# Revit family: 0005337
name_source: partatom
category: Lighting Fixtures
revit_build: Autodesk Revit 2017 (Build: 20190507_1515(x64)
units: mm (PartAtom-declared; Revit-internal decimal feet)

## family parameters
Cut with Voids When Loaded = No
Host = Face
Light Source = No
OmniClass Number = 23.80.70.00
OmniClass Title = Lighting
Part Type = Normal
Room Calculation Point = No
Round Connector Dimension = Use Diameter
Shared = No

## types (4) — shared parameters
Apparent Load = 0 VA
Assembly Code = D5020200
AssetType = Fixed
ClassificationName = Uniclass2015
ClassificationValue = EF_70_80
Default Elevation = 1219 mm
DocumentationLiterature = http://www.sylvania-lighting.com
IfcExportAs = IfcLightFixtureType
IfcExportType = IfcLightFixtureType
ImpactProtectionIndex = IK03
IngressProtection = IP20
InputNominalFrequency = 50/60 Hz
InputVoltage = 220-240 V AC
Keynote = 16500
Lamp = LED
LampColourRenderingIndex = 90
LampMacAdamStep = 3
LampsType = LED
Manufacturer = Feilo Sylvania
ManufacturerName = Feilo Sylvania
Material = aluminium housing
Material_1_SYL = PC/ABS Plastic
Material_2_SYL = <By Category>
Material_3_SYL = <By Category>
Material_4_SYL = <By Category>
NominalDepth = 180 mm
NominalLength = 180 mm
PowerFactor = 0.9
RadiusTrim_SYL = 90 mm  [stored 0.295276 ft]
RecessDepth_SYL = 100 mm  [stored 0.328084 ft]
RecessRadius_SYL = 83 mm
TrimHeight_SYL = 3 mm  [stored 0.00984252 ft]
Type Image = <None>
URL = http://www.sylvania-lighting.com
Voltage = 230 V
zero-valued in all types: Cost, NominalHeight

## per-type parameters (varying)
| type | LampColourTemperature | LampNominalLuminous | LuminousEfficacy | Model | ModelNumber | ModelReference | Name | PowerConsumption | TypeLamp_SYL | TypeName |
| 0005337+0005334 Ludospot 111 Hous Rnd 180mm Cardan WHT + Ludospot 111 3550lm 940 MB | 4000 K | 3550 lm | 93 lm/W | Ludospot 111 Hous Rnd 180mm Cardan WHT + Ludospot 111 3550lm 940 MB | 0005337+0005334 | Ludospot 111 Hous Rnd 180mm Cardan WHT + Ludospot 111 3550lm 940 MB | Ludospot 111 Hous Rnd 180mm Cardan WHT + Ludospot 111 3550lm 940 MB | 38 W | Ludospot 111 Modules : 0005334 Ludospot 111 3550lm 940 MB | Ludospot 111 Hous Rnd 180mm Cardan WHT + Ludospot 111 3550lm 940 MB |
| 0005337+0005333 Ludospot 111 Hous Rnd 180mm Cardan WHT + Ludospot 111 3500lm 930 MB | 3000 K | 3500 lm | 92 lm/W | Ludospot 111 Hous Rnd 180mm Cardan WHT + Ludospot 111 3500lm 930 MB | 0005337+0005333 | Ludospot 111 Hous Rnd 180mm Cardan WHT + Ludospot 111 3500lm 930 MB | Ludospot 111 Hous Rnd 180mm Cardan WHT + Ludospot 111 3500lm 930 MB | 38 W | Ludospot 111 Modules : 0005333 Ludospot 111 3500lm 930 MB | Ludospot 111 Hous Rnd 180mm Cardan WHT + Ludospot 111 3500lm 930 MB |
| 0005337+0005332 Ludospot 111 Hous Rnd 180mm Cardan WHT + Ludospot 111 2225lm 940 MB | 4000 K | 2225 lm | 93 lm/W | Ludospot 111 Hous Rnd 180mm Cardan WHT + Ludospot 111 2225lm 940 MB | 0005337+0005332 | Ludospot 111 Hous Rnd 180mm Cardan WHT + Ludospot 111 2225lm 940 MB | Ludospot 111 Hous Rnd 180mm Cardan WHT + Ludospot 111 2225lm 940 MB | 24 W | Ludospot 111 Modules : 0005332 Ludospot 111 2225lm 940 MB | Ludospot 111 Hous Rnd 180mm Cardan WHT + Ludospot 111 2225lm 940 MB |
| 0005337+0005331 Ludospot 111 Hous Rnd 180mm Cardan WHT + Ludospot 111 2025lm 930 MB | 3000 K | 2025 lm | 84 lm/W | Ludospot 111 Hous Rnd 180mm Cardan WHT + Ludospot 111 2025lm 930 MB | 0005337+0005331 | Ludospot 111 Hous Rnd 180mm Cardan WHT + Ludospot 111 2025lm 930 MB | Ludospot 111 Hous Rnd 180mm Cardan WHT + Ludospot 111 2025lm 930 MB | 24 W | Ludospot 111 Modules : 0005331 Ludospot 111 2025lm 930 MB | Ludospot 111 Hous Rnd 180mm Cardan WHT + Ludospot 111 2025lm 930 MB |

note: [stored X ft] marks values corroborated as IEEE doubles in the binary element streams (Revit-internal decimal feet)

## geometry (parser evidence)
native form markers: Sweep x6
no freeform markers — native parametric forms only
